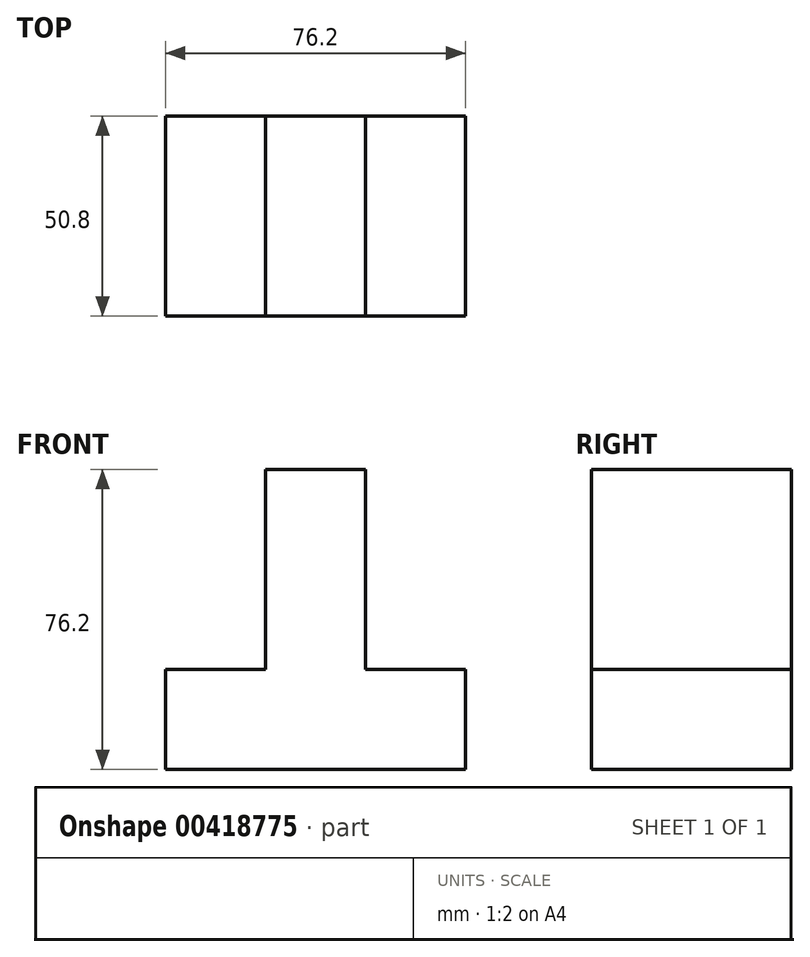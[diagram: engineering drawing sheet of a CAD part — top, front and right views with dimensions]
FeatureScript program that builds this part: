
annotation { "Feature Type Name" : "Feature", "Feature Type Description" : "" }
export const myFeature = defineFeature(function(context is Context, id is Id, definition is map)
    precondition{}
    {
        {
            var Q0;
            Q0=qCreatedBy(makeId("Front.planeOp"),FACE);
            var sketch = newSketch(context, id + "F0", { "sketchPlane" : qUnion([Q0])});
            skLineSegment(sketch, "E0", {"start": v(0, 0) * mm, "end": v(-76.2, 0) * mm});
            skLineSegment(sketch, "E1", {"start": v(-76.2, 0) * mm, "end": v(-76.2, 25.4) * mm});
            skLineSegment(sketch, "E2", {"start": v(-76.2, 25.4) * mm, "end": v(-50.8, 25.4) * mm});
            skLineSegment(sketch, "E3", {"start": v(-50.8, 25.4) * mm, "end": v(-50.8, 76.2) * mm});
            skLineSegment(sketch, "E4", {"start": v(-50.8, 76.2) * mm, "end": v(-25.4, 76.2) * mm});
            skLineSegment(sketch, "E5", {"start": v(-25.4, 76.2) * mm, "end": v(-25.4, 25.4) * mm});
            skLineSegment(sketch, "E6", {"start": v(-25.4, 25.4) * mm, "end": v(0, 25.4) * mm});
            skLineSegment(sketch, "E7", {"start": v(0, 25.4) * mm, "end": v(0, 0) * mm});
            skSolve(sketch);
        }
        {
            var Q0;
            Q0 = qSketchRegion(id + "F0", true);
            extrude(context, id + "F1", {"entities" : qUnion([Q0]), "depth" : 50.8 * mm});
        }
    });
